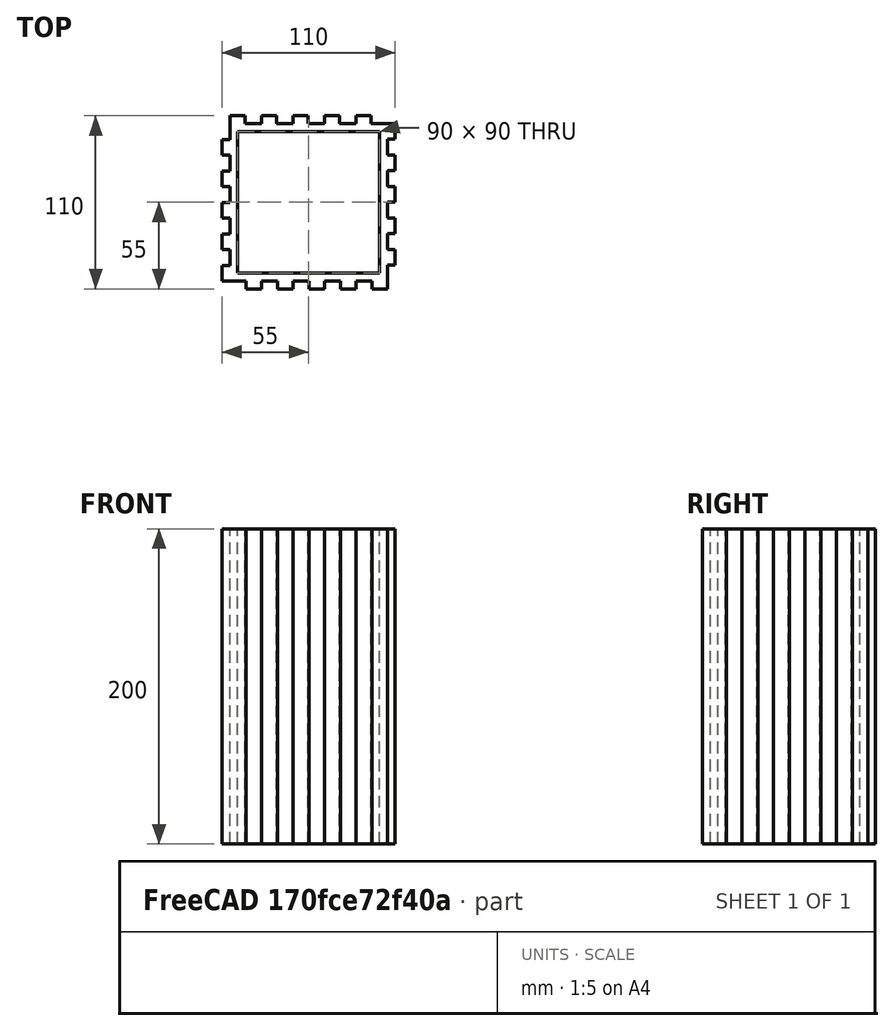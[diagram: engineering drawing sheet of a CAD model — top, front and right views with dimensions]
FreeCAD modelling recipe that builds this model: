
FCSTD DOCUMENT  (FreeCAD 0.21R33771 (Git))
Label: InterlockingBox
License: All rights reserved
LicenseURL: https://en.wikipedia.org/wiki/All_rights_reserved
objects: Sketcher::SketchObject×1, PartDesign::Pad×1, PartDesign::Body×1
note: 4 computed .brp shape members not serialized (recipe doc carries the construction recipe); baked Part::Feature solids carry a one-line shape summary decoded from their .brp

FEATURE [Sketcher::SketchObject] Sketch  label="BoxS"
  FullyConstrained = true
  MapMode = 5
  Support = -> [XY_Plane]
  sketch-geometry (94):
    g0: LineSegment StartX=50 StartY=-50 StartZ=0 EndX=50 EndY=50 EndZ=0
    g1: LineSegment StartX=50 StartY=50 StartZ=0 EndX=-50 EndY=50 EndZ=0
    g2: LineSegment StartX=-50 StartY=50 StartZ=0 EndX=-50 EndY=-50 EndZ=0
    g3: LineSegment StartX=-50 StartY=-50 StartZ=0 EndX=50 EndY=-50 EndZ=0
    g4: GeomPoint X=0 Y=0 Z=0
    g5: LineSegment StartX=-50 StartY=55 StartZ=0 EndX=-40.25 EndY=55 EndZ=0
    g6: LineSegment StartX=-40.25 StartY=55 StartZ=0 EndX=-40.25 EndY=50 EndZ=0
    g7: LineSegment StartX=-40.25 StartY=50 StartZ=0 EndX=-30 EndY=50 EndZ=0
    g8: LineSegment StartX=-30 StartY=50 StartZ=0 EndX=-30 EndY=55 EndZ=0
    g9: LineSegment StartX=-30 StartY=55 StartZ=0 EndX=-20.25 EndY=55 EndZ=0
    g10: LineSegment StartX=-20.25 StartY=55 StartZ=0 EndX=-20.25 EndY=50 EndZ=0
    g11: LineSegment StartX=10 StartY=50 StartZ=0 EndX=10 EndY=55 EndZ=0
    g12: LineSegment StartX=10 StartY=55 StartZ=0 EndX=19.75 EndY=55 EndZ=0
    g13: LineSegment StartX=19.75 StartY=55 StartZ=0 EndX=19.75 EndY=50 EndZ=0
    g14: LineSegment StartX=19.75 StartY=50 StartZ=0 EndX=30 EndY=50 EndZ=0
    g15: LineSegment StartX=30 StartY=50 StartZ=0 EndX=30 EndY=55 EndZ=0
    g16: LineSegment StartX=30 StartY=55 StartZ=0 EndX=39.75 EndY=55 EndZ=0
    g17: LineSegment StartX=39.75 StartY=55 StartZ=0 EndX=39.75 EndY=50 EndZ=0
    g18: LineSegment StartX=39.75 StartY=50 StartZ=0 EndX=50 EndY=50 EndZ=0
    g19: LineSegment StartX=55 StartY=50 StartZ=0 EndX=55 EndY=40.25 EndZ=0
    g20: LineSegment StartX=55 StartY=40.25 StartZ=0 EndX=50 EndY=40.25 EndZ=0
    g21: LineSegment StartX=50 StartY=40.25 StartZ=0 EndX=50 EndY=30 EndZ=0
    g22: LineSegment StartX=50 StartY=30 StartZ=0 EndX=55 EndY=30 EndZ=0
    g23: LineSegment StartX=55 StartY=30 StartZ=0 EndX=55 EndY=20.25 EndZ=0
    g24: LineSegment StartX=55 StartY=20.25 StartZ=0 EndX=50 EndY=20.25 EndZ=0
    g25: LineSegment StartX=50 StartY=-10 StartZ=0 EndX=55 EndY=-10 EndZ=0
    g26: LineSegment StartX=55 StartY=-10 StartZ=0 EndX=55 EndY=-19.75 EndZ=0
    g27: LineSegment StartX=55 StartY=-19.75 StartZ=0 EndX=50 EndY=-19.75 EndZ=0
    g28: LineSegment StartX=50 StartY=-19.75 StartZ=0 EndX=50 EndY=-30 EndZ=0
    g29: LineSegment StartX=50 StartY=-30 StartZ=0 EndX=55 EndY=-30 EndZ=0
    g30: LineSegment StartX=55 StartY=-30 StartZ=0 EndX=55 EndY=-39.75 EndZ=0
    g31: LineSegment StartX=55 StartY=-39.75 StartZ=0 EndX=50 EndY=-39.75 EndZ=0
    g32: LineSegment StartX=50 StartY=-39.75 StartZ=0 EndX=50 EndY=-50 EndZ=0
    g33: LineSegment StartX=50 StartY=-55 StartZ=0 EndX=40.25 EndY=-55 EndZ=0
    g34: LineSegment StartX=40.25 StartY=-55 StartZ=0 EndX=40.25 EndY=-50 EndZ=0
    g35: LineSegment StartX=40.25 StartY=-50 StartZ=0 EndX=30 EndY=-50 EndZ=0
    g36: LineSegment StartX=30 StartY=-50 StartZ=0 EndX=30 EndY=-55 EndZ=0
    g37: LineSegment StartX=30 StartY=-55 StartZ=0 EndX=20.25 EndY=-55 EndZ=0
    g38: LineSegment StartX=20.25 StartY=-55 StartZ=0 EndX=20.25 EndY=-50 EndZ=0
    g39: LineSegment StartX=-10 StartY=-50 StartZ=0 EndX=-10 EndY=-55 EndZ=0
    g40: LineSegment StartX=-10 StartY=-55 StartZ=0 EndX=-19.75 EndY=-55 EndZ=0
    g41: LineSegment StartX=-19.75 StartY=-55 StartZ=0 EndX=-19.75 EndY=-50 EndZ=0
    g42: LineSegment StartX=-19.75 StartY=-50 StartZ=0 EndX=-30 EndY=-50 EndZ=0
    g43: LineSegment StartX=-30 StartY=-50 StartZ=0 EndX=-30 EndY=-55 EndZ=0
    g44: LineSegment StartX=-30 StartY=-55 StartZ=0 EndX=-39.75 EndY=-55 EndZ=0
    g45: LineSegment StartX=-39.75 StartY=-55 StartZ=0 EndX=-39.75 EndY=-50 EndZ=0
    g46: LineSegment StartX=-39.75 StartY=-50 StartZ=0 EndX=-50 EndY=-50 EndZ=0
    g47: LineSegment StartX=-55 StartY=-50 StartZ=0 EndX=-55 EndY=-40.25 EndZ=0
    g48: LineSegment StartX=-55 StartY=-40.25 StartZ=0 EndX=-50 EndY=-40.25 EndZ=0
    g49: LineSegment StartX=-50 StartY=-40.25 StartZ=0 EndX=-50 EndY=-30 EndZ=0
    g50: LineSegment StartX=-50 StartY=-30 StartZ=0 EndX=-55 EndY=-30 EndZ=0
    g51: LineSegment StartX=-55 StartY=-30 StartZ=0 EndX=-55 EndY=-20.25 EndZ=0
    g52: LineSegment StartX=-55 StartY=-20.25 StartZ=0 EndX=-50 EndY=-20.25 EndZ=0
    g53: LineSegment StartX=-50 StartY=10 StartZ=0 EndX=-55 EndY=10 EndZ=0
    g54: LineSegment StartX=-55 StartY=10 StartZ=0 EndX=-55 EndY=19.75 EndZ=0
    g55: LineSegment StartX=-55 StartY=19.75 StartZ=0 EndX=-50 EndY=19.75 EndZ=0
    g56: LineSegment StartX=-50 StartY=19.75 StartZ=0 EndX=-50 EndY=30 EndZ=0
    g57: LineSegment StartX=-50 StartY=30 StartZ=0 EndX=-55 EndY=30 EndZ=0
    g58: LineSegment StartX=-55 StartY=30 StartZ=0 EndX=-55 EndY=39.75 EndZ=0
    g59: LineSegment StartX=-55 StartY=39.75 StartZ=0 EndX=-50 EndY=39.75 EndZ=0
    g60: LineSegment StartX=-50 StartY=39.75 StartZ=0 EndX=-50 EndY=50 EndZ=0
    g61: LineSegment StartX=-55 StartY=55 StartZ=0 EndX=55 EndY=55 EndZ=0
    g62: LineSegment StartX=55 StartY=55 StartZ=0 EndX=55 EndY=-55 EndZ=0
    g63: LineSegment StartX=55 StartY=-55 StartZ=0 EndX=-55 EndY=-55 EndZ=0
    g64: LineSegment StartX=-55 StartY=-55 StartZ=0 EndX=-55 EndY=55 EndZ=0
    g65: LineSegment StartX=-20.25 StartY=50 StartZ=0 EndX=-10 EndY=50 EndZ=0
    g66: LineSegment StartX=-10 StartY=50 StartZ=0 EndX=-10 EndY=55 EndZ=0
    g67: LineSegment StartX=-10 StartY=55 StartZ=0 EndX=-0.25 EndY=55 EndZ=0
    g68: LineSegment StartX=-0.25 StartY=55 StartZ=0 EndX=-0.25 EndY=50 EndZ=0
    g69: LineSegment StartX=-0.25 StartY=50 StartZ=0 EndX=10 EndY=50 EndZ=0
    g70: LineSegment StartX=50 StartY=20.25 StartZ=0 EndX=50 EndY=10 EndZ=0
    g71: LineSegment StartX=50 StartY=10 StartZ=0 EndX=55 EndY=10 EndZ=0
    g72: LineSegment StartX=55 StartY=10 StartZ=0 EndX=55 EndY=0.25 EndZ=0
    g73: LineSegment StartX=55 StartY=0.25 StartZ=0 EndX=50 EndY=0.25 EndZ=0
    g74: LineSegment StartX=50 StartY=0.25 StartZ=0 EndX=50 EndY=-10 EndZ=0
    g75: LineSegment StartX=-10 StartY=-50 StartZ=0 EndX=0.25 EndY=-50 EndZ=0
    g76: LineSegment StartX=0.25 StartY=-50 StartZ=0 EndX=0.25 EndY=-55 EndZ=0
    g77: LineSegment StartX=0.25 StartY=-55 StartZ=0 EndX=10 EndY=-55 EndZ=0
    g78: LineSegment StartX=10 StartY=-55 StartZ=0 EndX=10 EndY=-50 EndZ=0
    g79: LineSegment StartX=10 StartY=-50 StartZ=0 EndX=20.25 EndY=-50 EndZ=0
    g80: LineSegment StartX=-50 StartY=10 StartZ=0 EndX=-50 EndY=-0.25 EndZ=0
    g81: LineSegment StartX=-50 StartY=-0.25 StartZ=0 EndX=-55 EndY=-0.25 EndZ=0
    g82: LineSegment StartX=-55 StartY=-0.25 StartZ=0 EndX=-55 EndY=-10 EndZ=0
    g83: LineSegment StartX=-55 StartY=-10 StartZ=0 EndX=-50 EndY=-10 EndZ=0
    g84: LineSegment StartX=-50 StartY=-10 StartZ=0 EndX=-50 EndY=-20.25 EndZ=0
    g85: LineSegment StartX=-45 StartY=-45 StartZ=0 EndX=-45 EndY=45 EndZ=0
    g86: LineSegment StartX=-45 StartY=45 StartZ=0 EndX=45 EndY=45 EndZ=0
    g87: LineSegment StartX=45 StartY=45 StartZ=0 EndX=45 EndY=-45 EndZ=0
    g88: LineSegment StartX=45 StartY=-45 StartZ=0 EndX=-45 EndY=-45 EndZ=0
    g89: GeomPoint X=0 Y=0 Z=0
    g90: LineSegment StartX=50 StartY=50 StartZ=0 EndX=55 EndY=50 EndZ=0
    g91: LineSegment StartX=50 StartY=-50 StartZ=0 EndX=50 EndY=-55 EndZ=0
    g92: LineSegment StartX=-50 StartY=-50 StartZ=0 EndX=-55 EndY=-50 EndZ=0
    g93: LineSegment StartX=-50 StartY=55 StartZ=0 EndX=-50 EndY=50 EndZ=0
  constraints (272):
    c: Coincident(g0,g1)
    c: Coincident(g1,g2)
    c: Coincident(g2,g3)
    c: Coincident(g3,g0)
    c: Horizontal(g1)
    c: Horizontal(g3)
    c: Vertical(g0)
    c: Vertical(g2)
    c: Symmetric(g1,g0,g4)
    c: Distance(g1) = 100
    c: Distance(g0) = 100
    c: Coincident(g4,g-1)
    c: Horizontal(g5)
    c: Coincident(g5,g6)
    c: Vertical(g6)
    c: Coincident(g6,g7)
    c: Horizontal(g7)
    c: Coincident(g7,g8)
    c: Vertical(g8)
    c: Coincident(g8,g9)
    c: Horizontal(g9)
    c: Coincident(g9,g10)
    c: Vertical(g10)
    c: Vertical(g11)
    c: Coincident(g11,g12)
    c: Horizontal(g12)
    c: Coincident(g12,g13)
    c: Vertical(g13)
    c: Coincident(g13,g14)
    c: Horizontal(g14)
    c: Coincident(g14,g15)
    c: Vertical(g15)
    c: Coincident(g15,g16)
    c: Horizontal(g16)
    c: Coincident(g16,g17)
    c: Vertical(g17)
    c: Coincident(g17,g18)
    c: Horizontal(g18)
    c: Vertical(g19)
    c: Coincident(g19,g20)
    c: Coincident(g20,g21)
    c: Vertical(g21)
    c: Coincident(g21,g22)
    c: Coincident(g22,g23)
    c: Coincident(g23,g24)
    c: Horizontal(g25)
    c: Coincident(g25,g26)
    c: Coincident(g26,g27)
    c: Horizontal(g27)
    c: Coincident(g27,g28)
    c: Coincident(g28,g29)
    c: Horizontal(g29)
    c: Coincident(g29,g30)
    c: Vertical(g30)
    c: Coincident(g30,g31)
    c: Horizontal(g31)
    c: Coincident(g31,g32)
    c: Vertical(g32)
    c: Coincident(g33,g34)
    c: Vertical(g34)
    c: Coincident(g34,g35)
    c: Horizontal(g35)
    c: Coincident(g35,g36)
    c: Vertical(g36)
    c: Coincident(g36,g37)
    c: Horizontal(g37)
    c: Coincident(g37,g38)
    c: Vertical(g38)
    c: Vertical(g39)
    c: Coincident(g39,g40)
    c: Horizontal(g40)
    c: Coincident(g40,g41)
    c: Vertical(g41)
    c: Coincident(g41,g42)
    c: Horizontal(g42)
    c: Coincident(g42,g43)
    c: Vertical(g43)
    c: Coincident(g43,g44)
    c: Coincident(g44,g45)
    c: Vertical(g45)
    c: Coincident(g45,g46)
    c: Horizontal(g46)
    c: Vertical(g47)
    c: Coincident(g47,g48)
    c: Horizontal(g48)
    c: Coincident(g48,g49)
    c: Vertical(g49)
    c: Coincident(g49,g50)
    c: Coincident(g50,g51)
    c: Vertical(g51)
    c: Coincident(g51,g52)
    c: Coincident(g53,g54)
    c: Vertical(g54)
    c: Coincident(g54,g55)
    c: Horizontal(g55)
    c: Coincident(g55,g56)
    c: Vertical(g56)
    c: Coincident(g56,g57)
    c: Horizontal(g57)
    c: Coincident(g57,g58)
    c: Vertical(g58)
    c: Coincident(g58,g59)
    c: Horizontal(g59)
    c: Coincident(g59,g60)
    c: Vertical(g60)
    c: Vertical(g28)
    c: Vertical(g26)
    c: Vertical(g23)
    c: Horizontal(g20)
    c: Horizontal(g24)
    c: Horizontal(g22)
    c: Horizontal(g33)
    c: Horizontal(g50)
    c: Horizontal(g52)
    c: Horizontal(g53)
    c: Coincident(g18,g0)
    c: Coincident(g32,g0)
    c: Horizontal(g44)
    c: Coincident(g46,g2)
    c: Coincident(g61,g62)
    c: Coincident(g62,g63)
    c: Coincident(g63,g64)
    c: Coincident(g64,g61)
    c: Horizontal(g61)
    c: Horizontal(g63)
    c: Vertical(g62)
    c: Vertical(g64)
    c: Distance(g9) = 9.75
    c: Distance(g5) = 9.75
    c: Distance(g19) = 9.75
    c: Distance(g23) = 9.75
    c: Distance(g33) = 9.75
    c: Distance(g37) = 9.75
    c: Distance(g47) = 9.75
    c: Distance(g51) = 9.75
    c: Distance(g12) = 9.75
    c: Distance(g16) = 9.75
    c: Distance(g26) = 9.75
    c: Distance(g30) = 9.75
    c: Distance(g40) = 9.75
    c: Distance(g44) = 9.75
    c: Distance(g54) = 9.75
    c: Distance(g58) = 9.75
    c: Horizontal(g65)
    c: Coincident(g65,g66)
    c: Vertical(g66)
    c: Coincident(g66,g67)
    c: Horizontal(g67)
    c: Coincident(g67,g68)
    c: Vertical(g68)
    c: Coincident(g68,g69)
    c: Horizontal(g69)
    c: Coincident(g10,g65)
    c: Coincident(g69,g11)
    c: Vertical(g70)
    c: Coincident(g70,g71)
    c: Horizontal(g71)
    c: Coincident(g71,g72)
    c: Coincident(g72,g73)
    c: Coincident(g73,g74)
    c: Vertical(g72)
    c: Vertical(g74)
    c: Horizontal(g73)
    c: Coincident(g70,g24)
    c: Coincident(g74,g25)
    c: Horizontal(g75)
    c: Coincident(g75,g76)
    c: Vertical(g76)
    c: Coincident(g76,g77)
    c: Horizontal(g77)
    c: Coincident(g77,g78)
    c: Vertical(g78)
    c: Coincident(g78,g79)
    c: Horizontal(g79)
    c: Coincident(g75,g39)
    c: Coincident(g38,g79)
    c: Vertical(g80)
    c: Coincident(g80,g81)
    c: Horizontal(g81)
    c: Coincident(g81,g82)
    c: Vertical(g82)
    c: Coincident(g82,g83)
    c: Horizontal(g83)
    c: Coincident(g83,g84)
    c: Vertical(g84)
    c: Coincident(g53,g80)
    c: Coincident(g52,g84)
    c: PointOnObject(g58,g64)
    c: PointOnObject(g54,g64)
    c: PointOnObject(g81,g64)
    c: PointOnObject(g51,g64)
    c: PointOnObject(g56,g2)
    c: PointOnObject(g83,g2)
    c: PointOnObject(g49,g2)
    c: PointOnObject(g47,g64)
    c: PointOnObject(g44,g63)
    c: PointOnObject(g42,g3)
    c: PointOnObject(g40,g63)
    c: PointOnObject(g39,g3)
    c: PointOnObject(g76,g63)
    c: PointOnObject(g78,g3)
    c: PointOnObject(g37,g63)
    c: PointOnObject(g35,g3)
    c: PointOnObject(g33,g63)
    c: PointOnObject(g30,g62)
    c: PointOnObject(g28,g0)
    c: PointOnObject(g26,g62)
    c: PointOnObject(g25,g0)
    c: PointOnObject(g72,g62)
    c: PointOnObject(g70,g0)
    c: PointOnObject(g23,g62)
    c: PointOnObject(g21,g0)
    c: PointOnObject(g19,g62)
    c: PointOnObject(g16,g61)
    c: PointOnObject(g14,g1)
    c: PointOnObject(g12,g61)
    c: PointOnObject(g11,g1)
    c: PointOnObject(g67,g61)
    c: PointOnObject(g65,g1)
    c: PointOnObject(g9,g61)
    c: PointOnObject(g7,g1)
    c: PointOnObject(g5,g61)
    c: Distance(g7) = 10.25
    c: Distance(g65) = 10.25
    c: Distance(g67) = 9.75
    c: Distance(g69) = 10.25
    c: Distance(g14) = 10.25
    c: Distance(g21) = 10.25
    c: Distance(g70) = 10.25
    c: Distance(g72) = 9.75
    c: Distance(g74) = 10.25
    c: Distance(g28) = 10.25
    c: Distance(g35) = 10.25
    c: Distance(g79) = 10.25
    c: Distance(g77) = 9.75
    c: Distance(g75) = 10.25
    c: Distance(g42) = 10.25
    c: Distance(g49) = 10.25
    c: Distance(g84) = 10.25
    c: Distance(g82) = 9.75
    c: Distance(g80) = 10.25
    c: PointOnObject(g53,g2)
    c: Distance(g56) = 10.25
    c: Coincident(g85,g86)
    c: Coincident(g86,g87)
    c: Coincident(g87,g88)
    c: Coincident(g88,g85)
    c: Horizontal(g86)
    c: Horizontal(g88)
    c: Vertical(g85)
    c: Vertical(g87)
    c: Symmetric(g86,g85,g89)
    c: Coincident(g89,g4)
    c: Distance(g87) = 90
    c: Distance(g86) = 90
    c: Coincident(g91,g32)
    c: Coincident(g92,g46)
    c: Coincident(g93,g60)
    c: Coincident(g18,g90)
    c: PointOnObject(g59,g2)
    c: Symmetric(g61,g62,g4)
    c: Distance(g61) = 110
    c: Distance(g62) = 110
    c: Distance(g46) = 10.25
    c: Distance(g60) = 10.25
    c: Distance(g18) = 10.25
    c: DistanceY(g47,g46) = 0
    c: Distance(g32) = 10.25
    c: Coincident(g93,g5)
    c: Coincident(g90,g19)
    c: Coincident(g91,g33)
    c: Coincident(g92,g47)
FEATURE [PartDesign::Pad] Pad  label="BoxP"
  Direction = (0,0,1)
  Length = 200
  Length2 = 10
  Profile = -> Sketch
  ReferenceAxis = -> Sketch [N_Axis]
  Type = 0
FEATURE [PartDesign::Body] Body  label="Box"
  Group = -> [Sketch,Pad]
  Origin = -> Origin
  Tip = -> Pad
